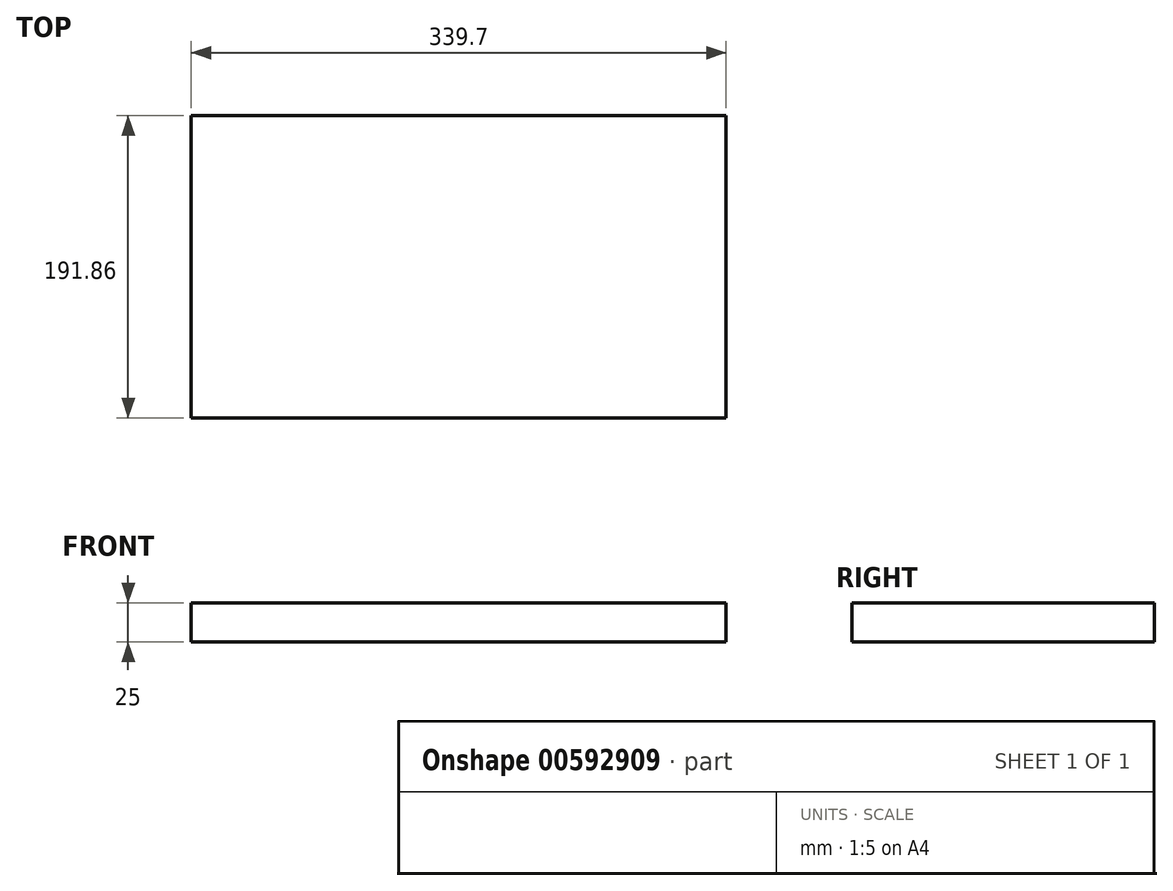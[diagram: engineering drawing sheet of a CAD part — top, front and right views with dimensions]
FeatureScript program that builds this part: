
annotation { "Feature Type Name" : "Feature", "Feature Type Description" : "" }
export const myFeature = defineFeature(function(context is Context, id is Id, definition is map)
    precondition{}
    {
        {
            var Q0;
            Q0=qCreatedBy(makeId("Top.planeOp"),FACE);
            var sketch = newSketch(context, id + "F0", { "sketchPlane" : qUnion([Q0])});
            skLineSegment(sketch, "E0.bottom", {"start": v(-169.85, 95.93) * mm, "end": v(169.85, 95.93) * mm});
            skLineSegment(sketch, "E0.top", {"start": v(-169.85, -95.93) * mm, "end": v(169.85, -95.93) * mm});
            skLineSegment(sketch, "E0.left", {"start": v(-169.85, 95.93) * mm, "end": v(-169.85, -95.93) * mm});
            skLineSegment(sketch, "E0.right", {"start": v(169.85, 95.93) * mm, "end": v(169.85, -95.93) * mm});
            skPoint(sketch, "E0.middle", {"position": v(0, 0) * mm});
            skSolve(sketch);
        }
        {
            var Q0;
            Q0=makeQuery(id+"F0.imprint","IMPRINT",FACE,{"disambiguationData":[TD([[makeQuery(id+"F0.imprint","IMPRINT",EDGE,{"derivedFrom":sQuery(id+"F0.wireOp",EDGE,"E0.bottom")}),-1.0]])]});
            extrude(context, id + "F1", {"entities" : qUnion([Q0]), "depth" : 25 * mm, "offsetDistance" : 25 * mm});
        }
    });
